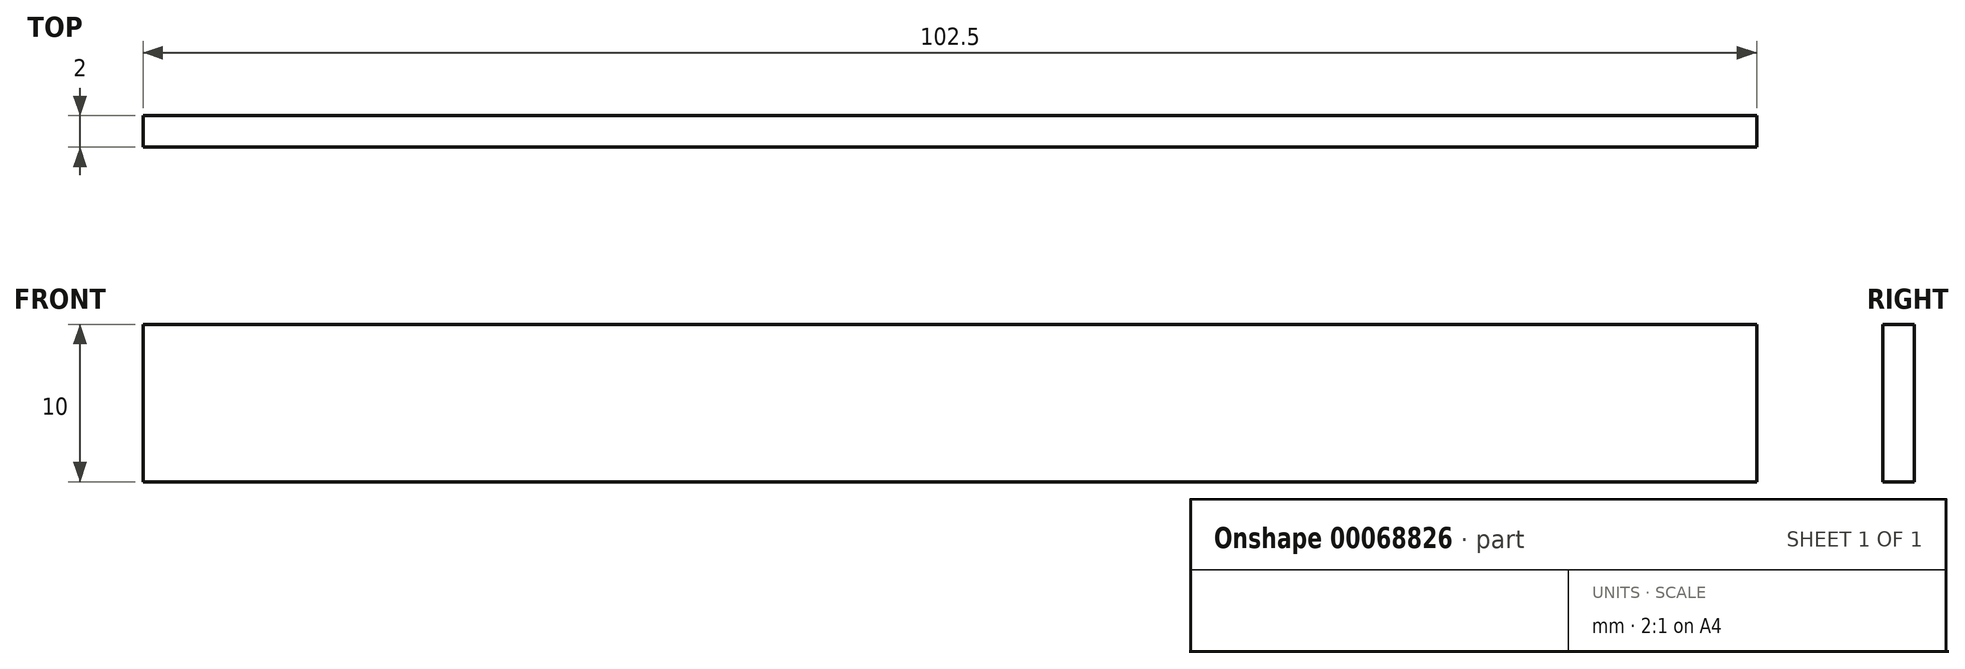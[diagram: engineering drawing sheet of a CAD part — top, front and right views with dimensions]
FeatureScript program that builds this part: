
annotation { "Feature Type Name" : "Feature", "Feature Type Description" : "" }
export const myFeature = defineFeature(function(context is Context, id is Id, definition is map)
    precondition{}
    {
        {
            var Q0;
            Q0=qCreatedBy(makeId("Front.planeOp"),FACE);
            var sketch = newSketch(context, id + "F0", { "sketchPlane" : qUnion([Q0])});
            skLineSegment(sketch, "E0.bottom", {"start": v(0, 0) * mm, "end": v(102.5, 0) * mm});
            skLineSegment(sketch, "E0.top", {"start": v(0, -10) * mm, "end": v(102.5, -10) * mm});
            skLineSegment(sketch, "E0.left", {"start": v(0, 0) * mm, "end": v(0, -10) * mm});
            skLineSegment(sketch, "E0.right", {"start": v(102.5, 0) * mm, "end": v(102.5, -10) * mm});
            skSolve(sketch);
        }
        {
            var Q0;
            Q0 = qSketchRegion(id + "F0", true);
            extrude(context, id + "F1", {"entities" : qUnion([Q0]), "depth" : 2 * mm});
        }
    });
